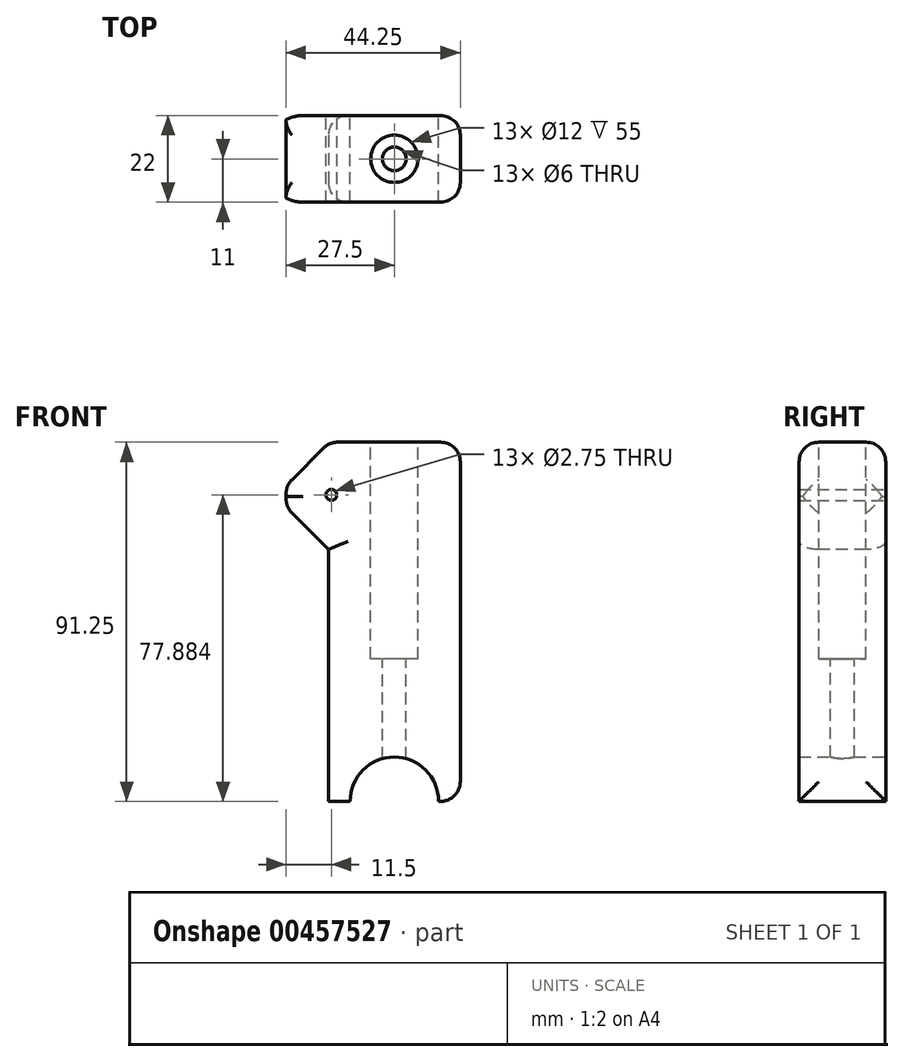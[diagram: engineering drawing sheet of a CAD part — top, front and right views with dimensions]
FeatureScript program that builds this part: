
annotation { "Feature Type Name" : "Feature", "Feature Type Description" : "" }
export const myFeature = defineFeature(function(context is Context, id is Id, definition is map)
    precondition{}
    {
        {
            var Q0;
            Q0=qCreatedBy(makeId("Front.planeOp"),FACE);
            var sketch = newSketch(context, id + "F0", { "sketchPlane" : qUnion([Q0])});
            skCircle(sketch, "E0", {"center": v(0, 0) * mm, "radius": 11.25 * mm});
            skCircle(sketch, "E1", {"center": v(0, 0) * mm, "radius": 16.75 * mm});
            skLineSegment(sketch, "E2", {"start": v(0, 11.25) * mm, "end": v(0, 36.25) * mm, "construction": true});
            skLineSegment(sketch, "E3.bottom", {"start": v(27.5, 36.25) * mm, "end": v(-27.5, 36.25) * mm});
            skLineSegment(sketch, "E3.top", {"start": v(27.5, -36.25) * mm, "end": v(-27.5, -36.25) * mm});
            skLineSegment(sketch, "E3.left", {"start": v(27.5, 36.25) * mm, "end": v(27.5, -36.25) * mm});
            skLineSegment(sketch, "E3.right", {"start": v(-27.5, 36.25) * mm, "end": v(-27.5, -36.25) * mm});
            skLineSegment(sketch, "E4", {"start": v(0, 36.25) * mm, "end": v(0, 91.25) * mm, "construction": true});
            skLineSegment(sketch, "E5.top", {"start": v(27.5, 91.25) * mm, "end": v(-27.5, 91.25) * mm});
            skLineSegment(sketch, "E5.left", {"start": v(27.5, 36.25) * mm, "end": v(27.5, 91.25) * mm});
            skLineSegment(sketch, "E5.right", {"start": v(-27.5, 36.25) * mm, "end": v(-27.5, 91.25) * mm});
            skPoint(sketch, "E5.middle", {"position": v(0, 63.75) * mm});
            skLineSegment(sketch, "E6", {"start": v(-27.5, 0) * mm, "end": v(27.5, 0) * mm});
            skLineSegment(sketch, "E7.bottom", {"start": v(-16.75, 63.75) * mm, "end": v(16.75, 63.75) * mm});
            skLineSegment(sketch, "E7.top", {"start": v(-16.75, -63.75) * mm, "end": v(16.75, -63.75) * mm});
            skLineSegment(sketch, "E7.left", {"start": v(-16.75, 63.75) * mm, "end": v(-16.75, -63.75) * mm});
            skLineSegment(sketch, "E7.right", {"start": v(16.75, 63.75) * mm, "end": v(16.75, -63.75) * mm});
            skLineSegment(sketch, "E8", {"start": v(-16.75, 63.75) * mm, "end": v(-27.5, 63.75) * mm});
            skLineSegment(sketch, "E9", {"start": v(16.75, 63.75) * mm, "end": v(27.5, 63.75) * mm});
            skLineSegment(sketch, "E10", {"start": v(16.75, 63.75) * mm, "end": v(16.75, 91.25) * mm});
            skLineSegment(sketch, "E11", {"start": v(0, 77.88) * mm, "end": v(-16, 77.88) * mm, "construction": true});
            skCircle(sketch, "E12", {"center": v(-16, 77.88) * mm, "radius": 1.38 * mm});
            skSolve(sketch);
        }
        {
            var Q0;
            {var subQ5=sQuery(id+"F0.wireOp",EDGE,"E7.bottom");Q0=makeQuery(id+"F0.imprint","IMPRINT",FACE,{"disambiguationData":[TD([[makeQuery(id+"F0.imprint","IMPRINT",EDGE,{"derivedFrom":subQ5}),-1.0]])]});}
            var Q1;
            {var subQ4=sQuery(id+"F0.wireOp",EDGE,"E7.right");var subQ6=sQuery(id+"F0.wireOp",EDGE,"E3.bottom");var subQ7=makeQuery(id+"F0.imprint","INTERSECT",VERTEX,{"derivedFrom":[subQ6,subQ4]});Q1=makeQuery(id+"F0.imprint","IMPRINT",FACE,{"disambiguationData":[TD([[makeQuery(id+"F0.imprint","IMPRINT",EDGE,{"disambiguationData":[TD([[subQ7,-1.0]])],"derivedFrom":subQ6}),1.0]])]});}
            var Q2;
            {var subQ0=sQuery(id+"F0.wireOp",EDGE,"E6");var subQ1=sQuery(id+"F0.wireOp",EDGE,"E0");var subQ2=makeQuery(id+"F0.imprint","INTERSECT",VERTEX,{"disambiguationData":[OD(0.0)],"derivedFrom":[subQ1,subQ0]});Q2=makeQuery(id+"F0.imprint","IMPRINT",FACE,{"disambiguationData":[TD([[makeQuery(id+"F0.imprint","IMPRINT",EDGE,{"disambiguationData":[TD([[subQ2,1.0]])],"derivedFrom":subQ1}),-1.0]])]});}
            var Q3;
            Q3=makeQuery(id+"F0.imprint","IMPRINT",FACE,{"disambiguationData":[TD([[makeQuery(id+"F0.imprint","IMPRINT",EDGE,{"derivedFrom":sQuery(id+"F0.wireOp",EDGE,"E7.bottom")}),1.0]])]});
            extrude(context, id + "F1", {"entities" : qUnion([Q0, Q1, Q2, Q3]), "endBound" : BoundingType.SYMMETRIC, "depth" : 22 * mm});
        }
        {
            var Q0;
            Q0=makeQuery(id+"F1.opExtrude","SWEPT_FACE",FACE,{"disambiguationData":[OSD([sQuery(id+"F0.wireOp",EDGE,"E5.top")])]});
            cPlane(context, id + "F2", {"entities" : qUnion([Q0]), "cplaneType" : CPlaneType.OFFSET, "offset" : 0 * mm, "width" : 150 * mm, "height" : 150 * mm});
        }
        {
            var Q0;
            Q0=qCreatedBy(id+"F2.planeOp",FACE);
            var sketch = newSketch(context, id + "F3", { "sketchPlane" : qUnion([Q0])});
            skCircle(sketch, "E13", {"center": v(0, 0) * mm, "radius": 6 * mm});
            skCircle(sketch, "E14", {"center": v(0, 0) * mm, "radius": 3 * mm});
            skSolve(sketch);
        }
        {
            var Q0;
            Q0=makeQuery(id+"F3.imprint","IMPRINT",FACE,{"disambiguationData":[TD([[makeQuery(id+"F3.imprint","IMPRINT",EDGE,{"derivedFrom":sQuery(id+"F3.wireOp",EDGE,"E13")}),1.0]])]});
            extrude(context, id + "F4", {"entities" : qUnion([Q0]), "operationType" : NewBodyOperationType.REMOVE, "oppositeDirection" : true, "depth" : 55 * mm});
        }
        {
            var Q0;
            Q0=makeQuery(id+"F3.imprint","IMPRINT",FACE,{"disambiguationData":[TD([[makeQuery(id+"F3.imprint","IMPRINT",EDGE,{"derivedFrom":sQuery(id+"F3.wireOp",EDGE,"E14")}),1.0]])]});
            extrude(context, id + "F5", {"entities" : qUnion([Q0]), "operationType" : NewBodyOperationType.REMOVE, "endBound" : BoundingType.THROUGH_ALL, "oppositeDirection" : true, "depth" : 25 * mm});
        }
        {
            var Q0;
            Q0=makeQuery(id+"F1.opExtrude","SWEPT_EDGE",EDGE,{"disambiguationData":[OSD([sQuery(id+"F0.wireOp",EDGE,"E5.right"),sQuery(id+"F0.wireOp",EDGE,"E8")])]});
            var Q1;
            Q1=makeQuery(id+"F1.opExtrude","SWEPT_EDGE",EDGE,{"disambiguationData":[OSD([sQuery(id+"F0.wireOp",EDGE,"E5.top"),sQuery(id+"F0.wireOp",EDGE,"E5.right")])]});
            chamfer(context, id + "F6", {"entities" : qUnion([Q0, Q1]), "width" : 11 * mm, "tangentPropagation" : true});
        }
        {
            var Q0;
            Q0=makeQuery(id+"F1.opExtrude","SWEPT_FACE",FACE,{"disambiguationData":[OSD([sQuery(id+"F0.wireOp",EDGE,"E7.right"),sQuery(id+"F0.wireOp",EDGE,"E10")])]});
            var Q1;
            Q1=makeQuery(id+"F1.opExtrude","CAP_EDGE",EDGE,{"disambiguationData":[OSD([sQuery(id+"F0.wireOp",EDGE,"E7.left")])],"isStart":false});
            var Q2;
            Q2=makeQuery(id+"F1.opExtrude","CAP_EDGE",EDGE,{"disambiguationData":[OSD([sQuery(id+"F0.wireOp",EDGE,"E7.left")])],"isStart":true});
            var Q3;
            {var subQ0=sQuery(id+"F0.wireOp",EDGE,"E5.right");Q3=makeQuery(id+"F6.opChamfer","BLEND_EDGE",EDGE,{"blendedFrom":[makeQuery(id+"F1.opExtrude","SWEPT_EDGE",EDGE,{"disambiguationData":[OSD([subQ0,sQuery(id+"F0.wireOp",EDGE,"E8")])]}),makeQuery(id+"F1.opExtrude","SWEPT_FACE",FACE,{"disambiguationData":[OSD([subQ0])]})],"blendedInto":[makeQuery(id+"F1.opExtrude","SWEPT_FACE",FACE,{"disambiguationData":[OSD([subQ0])]})]});}
            var Q4;
            {var subQ0=sQuery(id+"F0.wireOp",EDGE,"E5.right");Q4=makeQuery(id+"F6.opChamfer","BLEND_EDGE",EDGE,{"blendedFrom":[makeQuery(id+"F1.opExtrude","SWEPT_EDGE",EDGE,{"disambiguationData":[OSD([sQuery(id+"F0.wireOp",EDGE,"E5.top"),subQ0])]}),makeQuery(id+"F1.opExtrude","SWEPT_FACE",FACE,{"disambiguationData":[OSD([subQ0])]})],"blendedInto":[makeQuery(id+"F1.opExtrude","SWEPT_FACE",FACE,{"disambiguationData":[OSD([subQ0])]})]});}
            var Q5;
            {var subQ2=sQuery(id+"F0.wireOp",EDGE,"E5.right");var subQ7=sQuery(id+"F0.wireOp",EDGE,"E5.top");Q5=makeQuery(id+"F6.opChamfer","BLEND_EDGE",EDGE,{"blendedFrom":[makeQuery(id+"F1.opExtrude","SWEPT_EDGE",EDGE,{"disambiguationData":[OSD([subQ7,subQ2])]}),makeQuery(id+"F4.boolean.opBoolean","SPLIT",FACE,{"disambiguationData":[TD([makeQuery(id+"F1.opExtrude","SWEPT_FACE",FACE,{"disambiguationData":[OSD([subQ2])]})])],"derivedFrom":makeQuery(id+"F1.opExtrude","SWEPT_FACE",FACE,{"disambiguationData":[OSD([subQ7])]})})],"blendedInto":[makeQuery(id+"F4.boolean.opBoolean","SPLIT",FACE,{"disambiguationData":[TD([makeQuery(id+"F1.opExtrude","SWEPT_FACE",FACE,{"disambiguationData":[OSD([subQ2])]})])],"derivedFrom":makeQuery(id+"F1.opExtrude","SWEPT_FACE",FACE,{"disambiguationData":[OSD([subQ7])]})})]});}
            var Q6;
            Q6=makeQuery(id+"F1.opExtrude","CAP_EDGE",EDGE,{"disambiguationData":[OSD([sQuery(id+"F0.wireOp",EDGE,"E5.top")])],"isStart":false});
            var Q7;
            {var subQ0=sQuery(id+"F0.wireOp",EDGE,"E5.right");var subQ1=sQuery(id+"F0.wireOp",EDGE,"E5.top");Q7=makeQuery(id+"F6.opChamfer","BLEND_EDGE",EDGE,{"blendedFrom":[makeQuery(id+"F1.opExtrude","SWEPT_EDGE",EDGE,{"disambiguationData":[OSD([subQ1,subQ0])]}),makeQuery(id+"F1.opExtrude","CAP_FACE",FACE,{"disambiguationData":[OSD([sQuery(id+"F0.wireOp",EDGE,"E0"),subQ1,subQ0,sQuery(id+"F0.wireOp",EDGE,"E6"),sQuery(id+"F0.wireOp",EDGE,"E7.left"),sQuery(id+"F0.wireOp",EDGE,"E7.right"),sQuery(id+"F0.wireOp",EDGE,"E8"),sQuery(id+"F0.wireOp",EDGE,"E10"),sQuery(id+"F0.wireOp",EDGE,"E12")])],"isStart":false})],"blendedInto":[makeQuery(id+"F1.opExtrude","CAP_FACE",FACE,{"disambiguationData":[OSD([sQuery(id+"F0.wireOp",EDGE,"E0"),subQ1,subQ0,sQuery(id+"F0.wireOp",EDGE,"E6"),sQuery(id+"F0.wireOp",EDGE,"E7.left"),sQuery(id+"F0.wireOp",EDGE,"E7.right"),sQuery(id+"F0.wireOp",EDGE,"E8"),sQuery(id+"F0.wireOp",EDGE,"E10"),sQuery(id+"F0.wireOp",EDGE,"E12")])],"isStart":false})]});}
            var Q8;
            {var subQ0=sQuery(id+"F0.wireOp",EDGE,"E8");var subQ1=sQuery(id+"F0.wireOp",EDGE,"E5.right");Q8=makeQuery(id+"F6.opChamfer","BLEND_EDGE",EDGE,{"blendedFrom":[makeQuery(id+"F1.opExtrude","SWEPT_EDGE",EDGE,{"disambiguationData":[OSD([subQ1,subQ0])]}),makeQuery(id+"F1.opExtrude","CAP_FACE",FACE,{"disambiguationData":[OSD([sQuery(id+"F0.wireOp",EDGE,"E0"),sQuery(id+"F0.wireOp",EDGE,"E5.top"),subQ1,sQuery(id+"F0.wireOp",EDGE,"E6"),sQuery(id+"F0.wireOp",EDGE,"E7.left"),sQuery(id+"F0.wireOp",EDGE,"E7.right"),subQ0,sQuery(id+"F0.wireOp",EDGE,"E10"),sQuery(id+"F0.wireOp",EDGE,"E12")])],"isStart":false})],"blendedInto":[makeQuery(id+"F1.opExtrude","CAP_FACE",FACE,{"disambiguationData":[OSD([sQuery(id+"F0.wireOp",EDGE,"E0"),sQuery(id+"F0.wireOp",EDGE,"E5.top"),subQ1,sQuery(id+"F0.wireOp",EDGE,"E6"),sQuery(id+"F0.wireOp",EDGE,"E7.left"),sQuery(id+"F0.wireOp",EDGE,"E7.right"),subQ0,sQuery(id+"F0.wireOp",EDGE,"E10"),sQuery(id+"F0.wireOp",EDGE,"E12")])],"isStart":false})]});}
            var Q9;
            {var subQ0=sQuery(id+"F0.wireOp",EDGE,"E8");var subQ1=sQuery(id+"F0.wireOp",EDGE,"E5.right");Q9=makeQuery(id+"F6.opChamfer","BLEND_EDGE",EDGE,{"blendedFrom":[makeQuery(id+"F1.opExtrude","SWEPT_EDGE",EDGE,{"disambiguationData":[OSD([subQ1,subQ0])]}),makeQuery(id+"F1.opExtrude","CAP_FACE",FACE,{"disambiguationData":[OSD([sQuery(id+"F0.wireOp",EDGE,"E0"),sQuery(id+"F0.wireOp",EDGE,"E5.top"),subQ1,sQuery(id+"F0.wireOp",EDGE,"E6"),sQuery(id+"F0.wireOp",EDGE,"E7.left"),sQuery(id+"F0.wireOp",EDGE,"E7.right"),subQ0,sQuery(id+"F0.wireOp",EDGE,"E10"),sQuery(id+"F0.wireOp",EDGE,"E12")])],"isStart":true})],"blendedInto":[makeQuery(id+"F1.opExtrude","CAP_FACE",FACE,{"disambiguationData":[OSD([sQuery(id+"F0.wireOp",EDGE,"E0"),sQuery(id+"F0.wireOp",EDGE,"E5.top"),subQ1,sQuery(id+"F0.wireOp",EDGE,"E6"),sQuery(id+"F0.wireOp",EDGE,"E7.left"),sQuery(id+"F0.wireOp",EDGE,"E7.right"),subQ0,sQuery(id+"F0.wireOp",EDGE,"E10"),sQuery(id+"F0.wireOp",EDGE,"E12")])],"isStart":true})]});}
            var Q10;
            {var subQ0=sQuery(id+"F0.wireOp",EDGE,"E5.right");var subQ1=sQuery(id+"F0.wireOp",EDGE,"E5.top");Q10=makeQuery(id+"F6.opChamfer","BLEND_EDGE",EDGE,{"blendedFrom":[makeQuery(id+"F1.opExtrude","SWEPT_EDGE",EDGE,{"disambiguationData":[OSD([subQ1,subQ0])]}),makeQuery(id+"F1.opExtrude","CAP_FACE",FACE,{"disambiguationData":[OSD([sQuery(id+"F0.wireOp",EDGE,"E0"),subQ1,subQ0,sQuery(id+"F0.wireOp",EDGE,"E6"),sQuery(id+"F0.wireOp",EDGE,"E7.left"),sQuery(id+"F0.wireOp",EDGE,"E7.right"),sQuery(id+"F0.wireOp",EDGE,"E8"),sQuery(id+"F0.wireOp",EDGE,"E10"),sQuery(id+"F0.wireOp",EDGE,"E12")])],"isStart":true})],"blendedInto":[makeQuery(id+"F1.opExtrude","CAP_FACE",FACE,{"disambiguationData":[OSD([sQuery(id+"F0.wireOp",EDGE,"E0"),subQ1,subQ0,sQuery(id+"F0.wireOp",EDGE,"E6"),sQuery(id+"F0.wireOp",EDGE,"E7.left"),sQuery(id+"F0.wireOp",EDGE,"E7.right"),sQuery(id+"F0.wireOp",EDGE,"E8"),sQuery(id+"F0.wireOp",EDGE,"E10"),sQuery(id+"F0.wireOp",EDGE,"E12")])],"isStart":true})]});}
            var Q11;
            Q11=makeQuery(id+"F1.opExtrude","CAP_EDGE",EDGE,{"disambiguationData":[OSD([sQuery(id+"F0.wireOp",EDGE,"E5.top")])],"isStart":true});
            fillet(context, id + "F7", {"entities" : qUnion([Q0, Q1, Q2, Q3, Q4, Q5, Q6, Q7, Q8, Q9, Q10, Q11]), "radius" : 5 * mm, "tangentPropagation" : true, "allowEdgeOverflow" : false});
        }
    });
